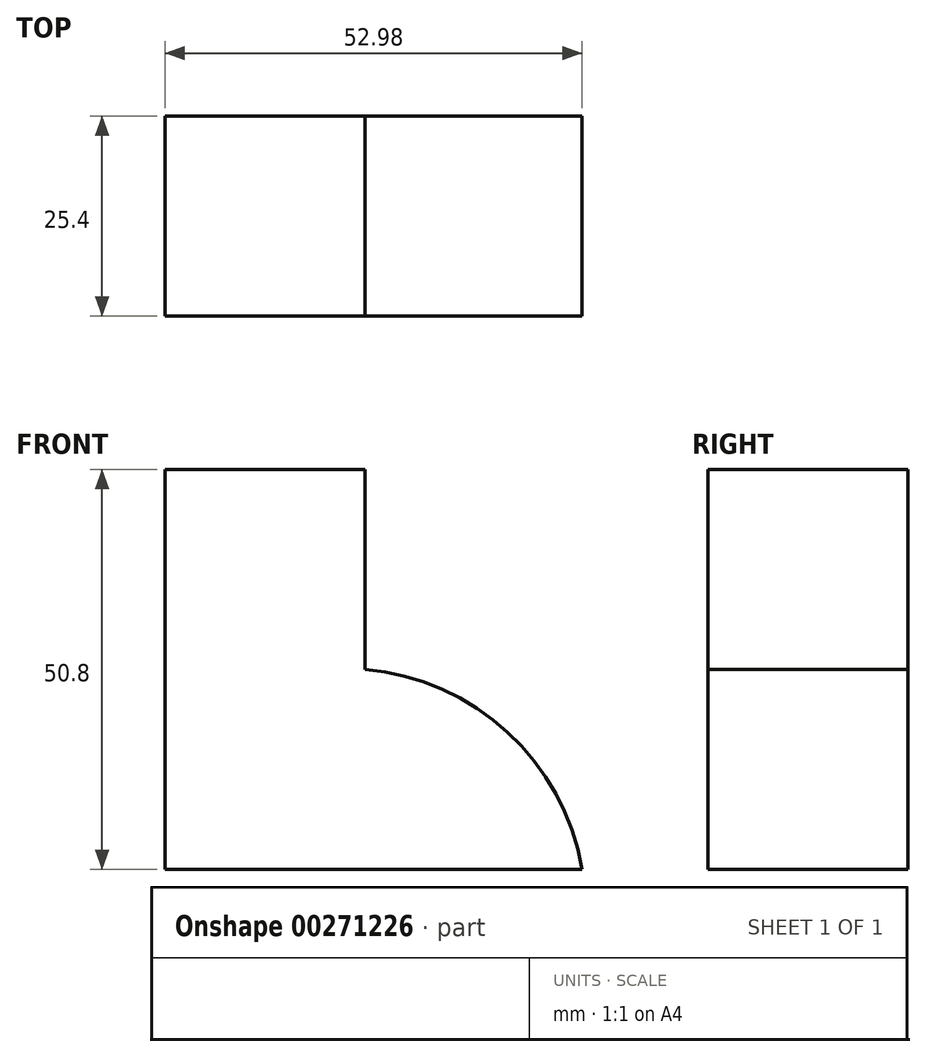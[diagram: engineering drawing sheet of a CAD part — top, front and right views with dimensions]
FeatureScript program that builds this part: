
annotation { "Feature Type Name" : "Feature", "Feature Type Description" : "" }
export const myFeature = defineFeature(function(context is Context, id is Id, definition is map)
    precondition{}
    {
        {
            var Q0;
            Q0=qCreatedBy(makeId("Front.planeOp"),FACE);
            var sketch = newSketch(context, id + "F0", { "sketchPlane" : qUnion([Q0])});
            skLineSegment(sketch, "E0.bottom", {"start": v(0, 0) * mm, "end": v(25.4, 0) * mm});
            skLineSegment(sketch, "E0.top", {"start": v(0, 50.8) * mm, "end": v(25.4, 50.8) * mm});
            skLineSegment(sketch, "E0.left", {"start": v(0, 0) * mm, "end": v(0, 50.8) * mm});
            skLineSegment(sketch, "E0.right", {"start": v(25.4, 0) * mm, "end": v(25.4, 50.8) * mm});
            skArc(sketch, "E1", {"start": v(52.98, 0) * mm, "mid": v(43.53, 17.41) * mm, "end": v(25.4, 25.4) * mm});
            skLineSegment(sketch, "E2", {"start": v(52.98, 0) * mm, "end": v(25.4, 0) * mm});
            skLineSegment(sketch, "E3", {"start": v(25.4, 25.4) * mm, "end": v(25.4, 0) * mm});
            skSolve(sketch);
        }
        {
            var Q0;
            Q0=makeQuery(id+"F0.imprint","IMPRINT",FACE,{"disambiguationData":[TD([[makeQuery(id+"F0.imprint","IMPRINT",EDGE,{"derivedFrom":sQuery(id+"F0.wireOp",EDGE,"E0.bottom")}),1.0]])]});
            var Q1;
            Q1=makeQuery(id+"F0.imprint","IMPRINT",FACE,{"disambiguationData":[TD([[makeQuery(id+"F0.imprint","IMPRINT",EDGE,{"derivedFrom":sQuery(id+"F0.wireOp",EDGE,"E1")}),1.0]])]});
            extrude(context, id + "F1", {"entities" : qUnion([Q0, Q1]), "depth" : 25.4 * mm});
        }
    });
